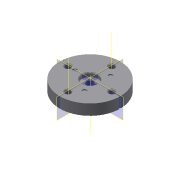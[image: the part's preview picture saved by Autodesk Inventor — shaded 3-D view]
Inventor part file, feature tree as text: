
AUTODESK INVENTOR PART (.ipt)
format: ipt  version: 2016 (Build 200138000, 138)  size: 522,240 bytes
history: native  units: mm
features: other x7, extrude x1, plane x1, sketch x1, projected_geometry x1
ambient origin geometry x8: Origin, YZ Plane, XZ Plane, XY Plane, X Axis, Y Axis, Z Axis, Center Point
bodies: Body1 (feature_tree)
feature tree (11):
  other  "Bryła1"
  other  "PRT0006.ipt1"
  other  "Oś konstrukcyjna1"
  other  "Płaszczyzna konstrukcyjna1"
  extrude  "Wyciągnięcie proste1"  Depth=0.06mm TaperAngle=0.0deg
  plane  "Work Plane2"
  other  "Baza1"
  sketch  "Szkic1"
  projected_geometry  "Pętla rzutowana1"
  other  "Work Axis2"
  other  "Work Axis3"
